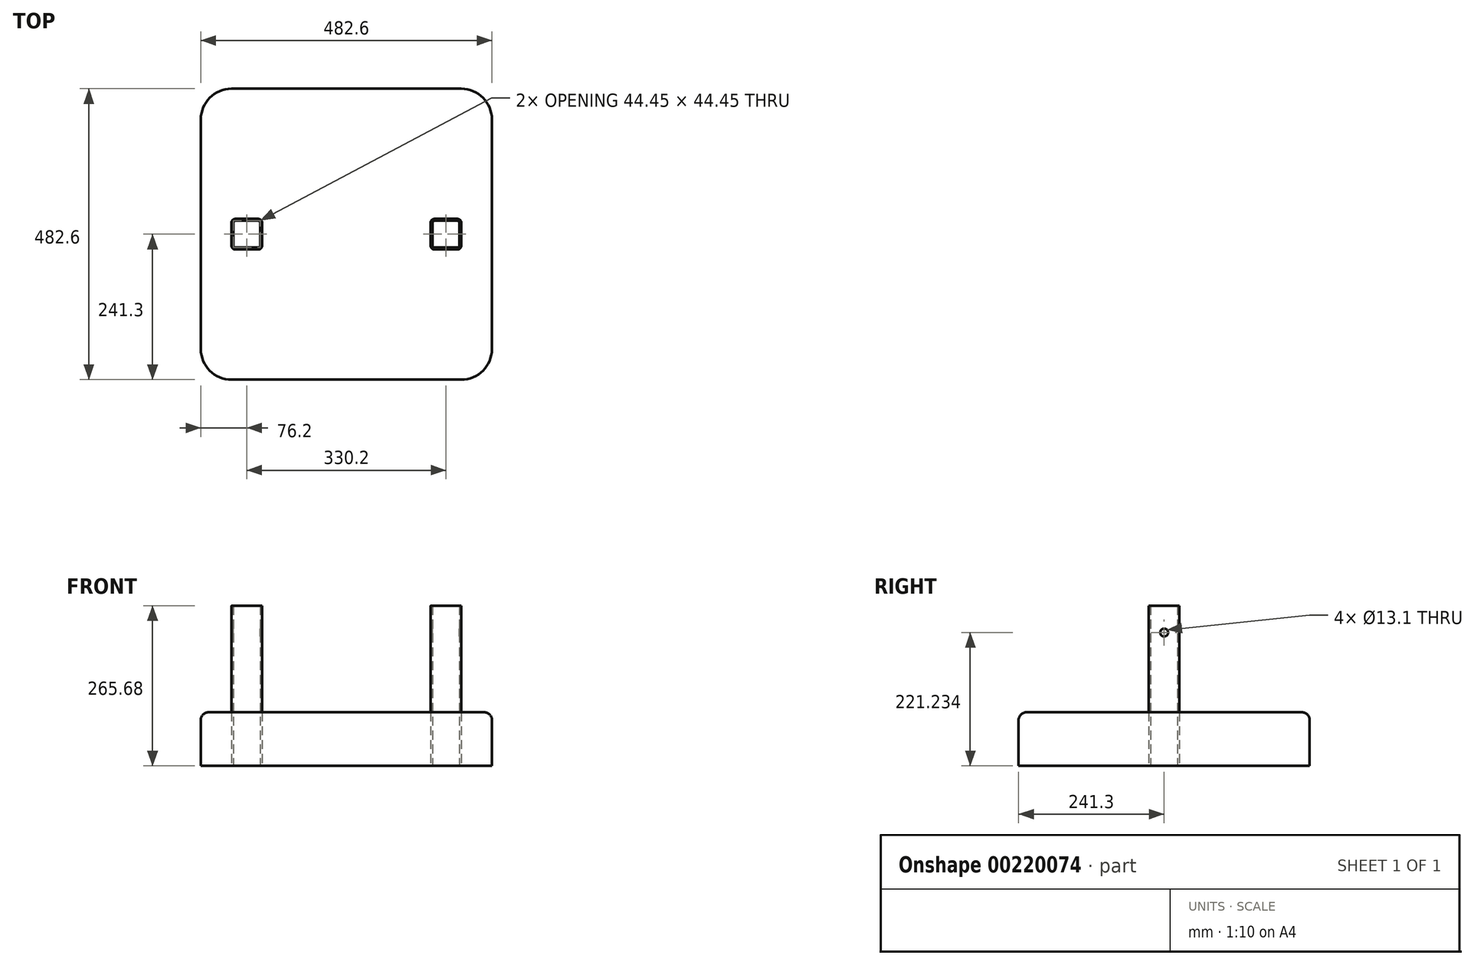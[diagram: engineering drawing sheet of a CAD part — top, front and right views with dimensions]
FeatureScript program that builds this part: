
annotation { "Feature Type Name" : "Feature", "Feature Type Description" : "" }
export const myFeature = defineFeature(function(context is Context, id is Id, definition is map)
    precondition{}
    {
        {
            var Q0;
            Q0=qCreatedBy(makeId("Top.planeOp"),FACE);
            var sketch = newSketch(context, id + "F0", { "sketchPlane" : qUnion([Q0])});
            skLineSegment(sketch, "E0.bottom", {"start": v(241.3, 241.3) * mm, "end": v(-241.3, 241.3) * mm});
            skLineSegment(sketch, "E0.top", {"start": v(241.3, -241.3) * mm, "end": v(-241.3, -241.3) * mm});
            skLineSegment(sketch, "E0.left", {"start": v(241.3, 241.3) * mm, "end": v(241.3, -241.3) * mm});
            skLineSegment(sketch, "E0.right", {"start": v(-241.3, 241.3) * mm, "end": v(-241.3, -241.3) * mm});
            skPoint(sketch, "E0.middle", {"position": v(0, 0) * mm});
            skSolve(sketch);
        }
        {
            var Q0;
            Q0 = qSketchRegion(id + "F0", true);
            extrude(context, id + "F1", {"entities" : qUnion([Q0]), "oppositeDirection" : true, "depth" : 88.9 * mm});
        }
        {
            var Q0;
            Q0=makeQuery(id+"F1.opExtrude","SWEPT_EDGE",EDGE,{"disambiguationData":[OSD([sQuery(id+"F0.wireOp",EDGE,"E0.top"),sQuery(id+"F0.wireOp",EDGE,"E0.right")])]});
            var Q1;
            Q1=makeQuery(id+"F1.opExtrude","SWEPT_EDGE",EDGE,{"disambiguationData":[OSD([sQuery(id+"F0.wireOp",EDGE,"E0.top"),sQuery(id+"F0.wireOp",EDGE,"E0.left")])]});
            var Q2;
            Q2=makeQuery(id+"F1.opExtrude","SWEPT_EDGE",EDGE,{"disambiguationData":[OSD([sQuery(id+"F0.wireOp",EDGE,"E0.bottom"),sQuery(id+"F0.wireOp",EDGE,"E0.left")])]});
            var Q3;
            Q3=makeQuery(id+"F1.opExtrude","SWEPT_EDGE",EDGE,{"disambiguationData":[OSD([sQuery(id+"F0.wireOp",EDGE,"E0.bottom"),sQuery(id+"F0.wireOp",EDGE,"E0.right")])]});
            fillet(context, id + "F2", {"entities" : qUnion([Q0, Q1, Q2, Q3]), "radius" : 50.8 * mm, "tangentPropagation" : true, "allowEdgeOverflow" : false});
        }
        {
            var Q0;
            Q0=makeQuery(id+"F1.opExtrude","CAP_EDGE",EDGE,{"disambiguationData":[OSD([sQuery(id+"F0.wireOp",EDGE,"E0.bottom")])],"isStart":true});
            fillet(context, id + "F3", {"entities" : qUnion([Q0]), "radius" : 12.7 * mm, "tangentPropagation" : true, "allowEdgeOverflow" : false});
        }
        {
            var Q0;
            Q0=qCreatedBy(makeId("Top.planeOp"),FACE);
            var sketch = newSketch(context, id + "F4", { "sketchPlane" : qUnion([Q0])});
            skLineSegment(sketch, "E1", {"start": v(0, 0) * mm, "end": v(122.39, 0) * mm, "construction": true});
            skLineSegment(sketch, "E2", {"start": v(0, 0) * mm, "end": v(-82.1, 0) * mm, "construction": true});
            skPoint(sketch, "E3.middle", {"position": v(165.1, 0) * mm});
            skLineSegment(sketch, "E4.bottom", {"start": v(184.15, 25.4) * mm, "end": v(146.05, 25.4) * mm});
            skLineSegment(sketch, "E4.top", {"start": v(184.15, -25.4) * mm, "end": v(146.05, -25.4) * mm});
            skLineSegment(sketch, "E4.left", {"start": v(190.5, 19.05) * mm, "end": v(190.5, -19.05) * mm});
            skLineSegment(sketch, "E4.right", {"start": v(139.7, 19.05) * mm, "end": v(139.7, -19.05) * mm});
            skLineSegment(sketch, "E5.0", {"start": v(184.15, 22.22) * mm, "end": v(146.05, 22.22) * mm});
            skLineSegment(sketch, "E5.1", {"start": v(187.33, 19.05) * mm, "end": v(187.33, -19.05) * mm});
            skLineSegment(sketch, "E5.2", {"start": v(184.15, -22.23) * mm, "end": v(146.05, -22.23) * mm});
            skLineSegment(sketch, "E5.3", {"start": v(142.88, 19.05) * mm, "end": v(142.88, -19.05) * mm});
            skPoint(sketch, "E6.visualSharp", {"position": v(139.7, 25.4) * mm});
            skArc(sketch, "E6.filletArc", {"start": v(146.05, 25.4) * mm, "mid": v(141.56, 23.54) * mm, "end": v(139.7, 19.05) * mm});
            skPoint(sketch, "E7.visualSharp", {"position": v(139.7, -25.4) * mm});
            skArc(sketch, "E7.filletArc", {"start": v(139.7, -19.05) * mm, "mid": v(141.56, -23.54) * mm, "end": v(146.05, -25.4) * mm});
            skPoint(sketch, "E8.visualSharp", {"position": v(190.5, -25.4) * mm});
            skArc(sketch, "E8.filletArc", {"start": v(184.15, -25.4) * mm, "mid": v(188.64, -23.54) * mm, "end": v(190.5, -19.05) * mm});
            skPoint(sketch, "E9.visualSharp", {"position": v(190.5, 25.4) * mm});
            skArc(sketch, "E9.filletArc", {"start": v(190.5, 19.05) * mm, "mid": v(188.64, 23.54) * mm, "end": v(184.15, 25.4) * mm});
            skPoint(sketch, "E10.visualSharp", {"position": v(142.88, 22.22) * mm});
            skArc(sketch, "E10.filletArc", {"start": v(146.05, 22.22) * mm, "mid": v(143.8, 21.3) * mm, "end": v(142.88, 19.05) * mm});
            skPoint(sketch, "E11.visualSharp", {"position": v(142.88, -22.23) * mm});
            skArc(sketch, "E11.filletArc", {"start": v(142.88, -19.05) * mm, "mid": v(143.8, -21.3) * mm, "end": v(146.05, -22.23) * mm});
            skPoint(sketch, "E12.visualSharp", {"position": v(187.33, 22.22) * mm});
            skArc(sketch, "E12.filletArc", {"start": v(187.33, 19.05) * mm, "mid": v(186.4, 21.3) * mm, "end": v(184.15, 22.22) * mm});
            skPoint(sketch, "E13.visualSharp", {"position": v(187.33, -22.23) * mm});
            skArc(sketch, "E13.filletArc", {"start": v(184.15, -22.22) * mm, "mid": v(186.4, -21.3) * mm, "end": v(187.32, -19.05) * mm});
            skArc(sketch, "E14.MirrorCS", {"start": v(-146.05, 22.22) * mm, "mid": v(-143.8, 21.3) * mm, "end": v(-142.88, 19.05) * mm});
            skArc(sketch, "E15.MirrorCS", {"start": v(-146.05, 25.4) * mm, "mid": v(-141.56, 23.54) * mm, "end": v(-139.7, 19.05) * mm});
            skArc(sketch, "E16.MirrorCS", {"start": v(-142.88, -19.05) * mm, "mid": v(-143.8, -21.3) * mm, "end": v(-146.05, -22.23) * mm});
            skArc(sketch, "E17.MirrorCS", {"start": v(-139.7, -19.05) * mm, "mid": v(-141.56, -23.54) * mm, "end": v(-146.05, -25.4) * mm});
            skArc(sketch, "E18.MirrorCS", {"start": v(-187.33, 19.05) * mm, "mid": v(-186.4, 21.3) * mm, "end": v(-184.15, 22.22) * mm});
            skArc(sketch, "E19.MirrorCS", {"start": v(-184.15, -25.4) * mm, "mid": v(-188.64, -23.54) * mm, "end": v(-190.5, -19.05) * mm});
            skArc(sketch, "E20.MirrorCS", {"start": v(-184.15, -22.22) * mm, "mid": v(-186.4, -21.3) * mm, "end": v(-187.32, -19.05) * mm});
            skArc(sketch, "E21.MirrorCS", {"start": v(-190.5, 19.05) * mm, "mid": v(-188.64, 23.54) * mm, "end": v(-184.15, 25.4) * mm});
            skPoint(sketch, "E22.MirrorP", {"position": v(-165.1, 0) * mm});
            skLineSegment(sketch, "E23.MirrorCS", {"start": v(-184.15, 22.22) * mm, "end": v(-146.05, 22.23) * mm});
            skLineSegment(sketch, "E24.MirrorCS", {"start": v(-184.15, 25.4) * mm, "end": v(-146.05, 25.4) * mm});
            skPoint(sketch, "E25.MirrorP", {"position": v(-139.7, -25.4) * mm});
            skLineSegment(sketch, "E26.MirrorCS", {"start": v(-184.15, -22.23) * mm, "end": v(-146.05, -22.23) * mm});
            skLineSegment(sketch, "E27.MirrorCS", {"start": v(-142.88, 19.05) * mm, "end": v(-142.88, -19.05) * mm});
            skLineSegment(sketch, "E28.MirrorCS", {"start": v(-187.33, 19.05) * mm, "end": v(-187.33, -19.05) * mm});
            skLineSegment(sketch, "E29.MirrorCS", {"start": v(-190.5, 19.05) * mm, "end": v(-190.5, -19.05) * mm});
            skLineSegment(sketch, "E30.MirrorCS", {"start": v(-139.7, 19.05) * mm, "end": v(-139.7, -19.05) * mm});
            skLineSegment(sketch, "E31.MirrorCS", {"start": v(-184.15, -25.4) * mm, "end": v(-146.05, -25.4) * mm});
            skPoint(sketch, "E32.MirrorP", {"position": v(-187.33, 22.22) * mm});
            skPoint(sketch, "E33.MirrorP", {"position": v(-142.88, -22.23) * mm});
            skPoint(sketch, "E34.MirrorP", {"position": v(-190.5, -25.4) * mm});
            skPoint(sketch, "E35.MirrorP", {"position": v(-139.7, 25.4) * mm});
            skPoint(sketch, "E36.MirrorP", {"position": v(-187.33, -22.23) * mm});
            skPoint(sketch, "E37.MirrorP", {"position": v(-190.5, 25.4) * mm});
            skPoint(sketch, "E38.MirrorP", {"position": v(-142.88, 22.22) * mm});
            skSolve(sketch);
        }
        {
            var Q0;
            Q0 = qSketchRegion(id + "F4", true);
            extrude(context, id + "F5", {"entities" : qUnion([Q0]), "endBound" : BoundingType.SYMMETRIC, "depth" : 177.8 * mm});
        }
        {
            var Q0;
            Q0=makeQuery(id+"F5.opExtrude","CAP_FACE",FACE,{"disambiguationData":[OSD([sQuery(id+"F4.wireOp",EDGE,"E4.bottom"),sQuery(id+"F4.wireOp",EDGE,"E4.top"),sQuery(id+"F4.wireOp",EDGE,"E4.left"),sQuery(id+"F4.wireOp",EDGE,"E4.right"),sQuery(id+"F4.wireOp",EDGE,"E5.0"),sQuery(id+"F4.wireOp",EDGE,"E5.1"),sQuery(id+"F4.wireOp",EDGE,"E5.2"),sQuery(id+"F4.wireOp",EDGE,"E5.3"),sQuery(id+"F4.wireOp",EDGE,"E6.filletArc"),sQuery(id+"F4.wireOp",EDGE,"E7.filletArc"),sQuery(id+"F4.wireOp",EDGE,"E8.filletArc"),sQuery(id+"F4.wireOp",EDGE,"E9.filletArc"),sQuery(id+"F4.wireOp",EDGE,"E10.filletArc"),sQuery(id+"F4.wireOp",EDGE,"E11.filletArc"),sQuery(id+"F4.wireOp",EDGE,"E12.filletArc"),sQuery(id+"F4.wireOp",EDGE,"E13.filletArc")])],"isStart":false});
            var sketch = newSketch(context, id + "F6", { "sketchPlane" : qUnion([Q0])});
            skLineSegment(sketch, "E39.0.0", {"start": v(146.05, -25.4) * mm, "end": v(184.15, -25.4) * mm});
            skArc(sketch, "E39.0.1", {"start": v(184.15, -25.4) * mm, "mid": v(188.64, -23.54) * mm, "end": v(190.5, -19.05) * mm});
            skLineSegment(sketch, "E39.0.2", {"start": v(190.5, -19.05) * mm, "end": v(190.5, 19.05) * mm});
            skArc(sketch, "E39.0.3", {"start": v(190.5, 19.05) * mm, "mid": v(188.64, 23.54) * mm, "end": v(184.15, 25.4) * mm});
            skLineSegment(sketch, "E39.0.4", {"start": v(184.15, 25.4) * mm, "end": v(146.05, 25.4) * mm});
            skArc(sketch, "E39.0.5", {"start": v(146.05, 25.4) * mm, "mid": v(141.56, 23.54) * mm, "end": v(139.7, 19.05) * mm});
            skLineSegment(sketch, "E39.0.6", {"start": v(139.7, 19.05) * mm, "end": v(139.7, -19.05) * mm});
            skArc(sketch, "E39.0.7", {"start": v(139.7, -19.05) * mm, "mid": v(141.56, -23.54) * mm, "end": v(146.05, -25.4) * mm});
            skLineSegment(sketch, "E40.0", {"start": v(142.88, 19.05) * mm, "end": v(142.88, -19.05) * mm});
            skPoint(sketch, "E41.0", {"position": v(143.8, 21.3) * mm});
            skLineSegment(sketch, "E42.0", {"start": v(184.15, 22.22) * mm, "end": v(146.05, 22.22) * mm});
            skPoint(sketch, "E43.0", {"position": v(186.4, 21.3) * mm});
            skLineSegment(sketch, "E44.0", {"start": v(187.33, 19.05) * mm, "end": v(187.33, -19.05) * mm});
            skPoint(sketch, "E45.0", {"position": v(186.4, -21.3) * mm});
            skLineSegment(sketch, "E46.0", {"start": v(184.15, -22.23) * mm, "end": v(146.05, -22.23) * mm});
            skPoint(sketch, "E47.0", {"position": v(143.8, -21.3) * mm});
            skArc(sketch, "E48.0", {"start": v(184.15, -22.22) * mm, "mid": v(186.4, -21.3) * mm, "end": v(187.32, -19.05) * mm});
            skArc(sketch, "E49.0", {"start": v(187.33, 19.05) * mm, "mid": v(186.4, 21.3) * mm, "end": v(184.15, 22.22) * mm});
            skArc(sketch, "E50.0", {"start": v(146.05, 22.23) * mm, "mid": v(143.8, 21.3) * mm, "end": v(142.88, 19.05) * mm});
            skArc(sketch, "E51.0", {"start": v(142.88, -19.05) * mm, "mid": v(143.8, -21.3) * mm, "end": v(146.05, -22.23) * mm});
            skArc(sketch, "E52.MirrorCS", {"start": v(-146.05, 22.22) * mm, "mid": v(-143.8, 21.3) * mm, "end": v(-142.88, 19.05) * mm});
            skArc(sketch, "E53.MirrorCS", {"start": v(-146.05, 25.4) * mm, "mid": v(-141.56, 23.54) * mm, "end": v(-139.7, 19.05) * mm});
            skArc(sketch, "E54.MirrorCS", {"start": v(-142.88, -19.05) * mm, "mid": v(-143.8, -21.3) * mm, "end": v(-146.05, -22.23) * mm});
            skArc(sketch, "E55.MirrorCS", {"start": v(-139.7, -19.05) * mm, "mid": v(-141.56, -23.54) * mm, "end": v(-146.05, -25.4) * mm});
            skArc(sketch, "E56.MirrorCS", {"start": v(-184.15, -25.4) * mm, "mid": v(-188.64, -23.54) * mm, "end": v(-190.5, -19.05) * mm});
            skArc(sketch, "E57.MirrorCS", {"start": v(-187.33, 19.05) * mm, "mid": v(-186.4, 21.3) * mm, "end": v(-184.15, 22.22) * mm});
            skArc(sketch, "E58.MirrorCS", {"start": v(-184.15, -22.22) * mm, "mid": v(-186.4, -21.3) * mm, "end": v(-187.32, -19.05) * mm});
            skArc(sketch, "E59.MirrorCS", {"start": v(-190.5, 19.05) * mm, "mid": v(-188.64, 23.54) * mm, "end": v(-184.15, 25.4) * mm});
            skLineSegment(sketch, "E60.MirrorCS", {"start": v(-146.05, -25.4) * mm, "end": v(-184.15, -25.4) * mm});
            skPoint(sketch, "E61.MirrorP", {"position": v(-143.8, -21.3) * mm});
            skPoint(sketch, "E62.MirrorP", {"position": v(-143.8, 21.3) * mm});
            skPoint(sketch, "E63.MirrorP", {"position": v(-186.4, -21.3) * mm});
            skLineSegment(sketch, "E64.MirrorCS", {"start": v(-184.15, -22.23) * mm, "end": v(-146.05, -22.23) * mm});
            skLineSegment(sketch, "E65.MirrorCS", {"start": v(-187.33, 19.05) * mm, "end": v(-187.33, -19.05) * mm});
            skLineSegment(sketch, "E66.MirrorCS", {"start": v(-184.15, 22.22) * mm, "end": v(-146.05, 22.23) * mm});
            skLineSegment(sketch, "E67.MirrorCS", {"start": v(-142.88, 19.05) * mm, "end": v(-142.88, -19.05) * mm});
            skPoint(sketch, "E68.MirrorP", {"position": v(-186.4, 21.3) * mm});
            skLineSegment(sketch, "E69.MirrorCS", {"start": v(-139.7, 19.05) * mm, "end": v(-139.7, -19.05) * mm});
            skLineSegment(sketch, "E70.MirrorCS", {"start": v(-190.5, -19.05) * mm, "end": v(-190.5, 19.05) * mm});
            skLineSegment(sketch, "E71.MirrorCS", {"start": v(-184.15, 25.4) * mm, "end": v(-146.05, 25.4) * mm});
            skSolve(sketch);
        }
        {
            var Q0;
            Q0 = qSketchRegion(id + "F6", true);
            extrude(context, id + "F7", {"entities" : qUnion([Q0]), "operationType" : NewBodyOperationType.ADD, "depth" : 87.88 * mm});
        }
        {
            var Q0;
            Q0=makeQuery(id+"F7.boolean.opBoolean","MERGE",FACE,{"derivedFrom":[makeQuery(id+"F5.opExtrude","SWEPT_FACE",FACE,{"disambiguationData":[OSD([sQuery(id+"F4.wireOp",EDGE,"E4.left")])]}),makeQuery(id+"F7.opExtrude","SWEPT_FACE",FACE,{"disambiguationData":[OSD([sQuery(id+"F6.wireOp",EDGE,"E39.0.2")])]})]});
            var sketch = newSketch(context, id + "F8", { "sketchPlane" : qUnion([Q0])});
            skLineSegment(sketch, "E72", {"start": v(0, 176.78) * mm, "end": v(0, 51.92) * mm, "construction": true});
            skPoint(sketch, "E72.endSnap0", {"position": v(0, 176.78) * mm});
            skCircle(sketch, "E73", {"center": v(0, 132.33) * mm, "radius": 6.55 * mm});
            skSolve(sketch);
        }
        {
            var Q0;
            Q0 = qSketchRegion(id + "F8", true);
            extrude(context, id + "F9", {"entities" : qUnion([Q0]), "operationType" : NewBodyOperationType.REMOVE, "endBound" : BoundingType.THROUGH_ALL, "oppositeDirection" : true, "depth" : 25.4 * mm});
        }
    });
